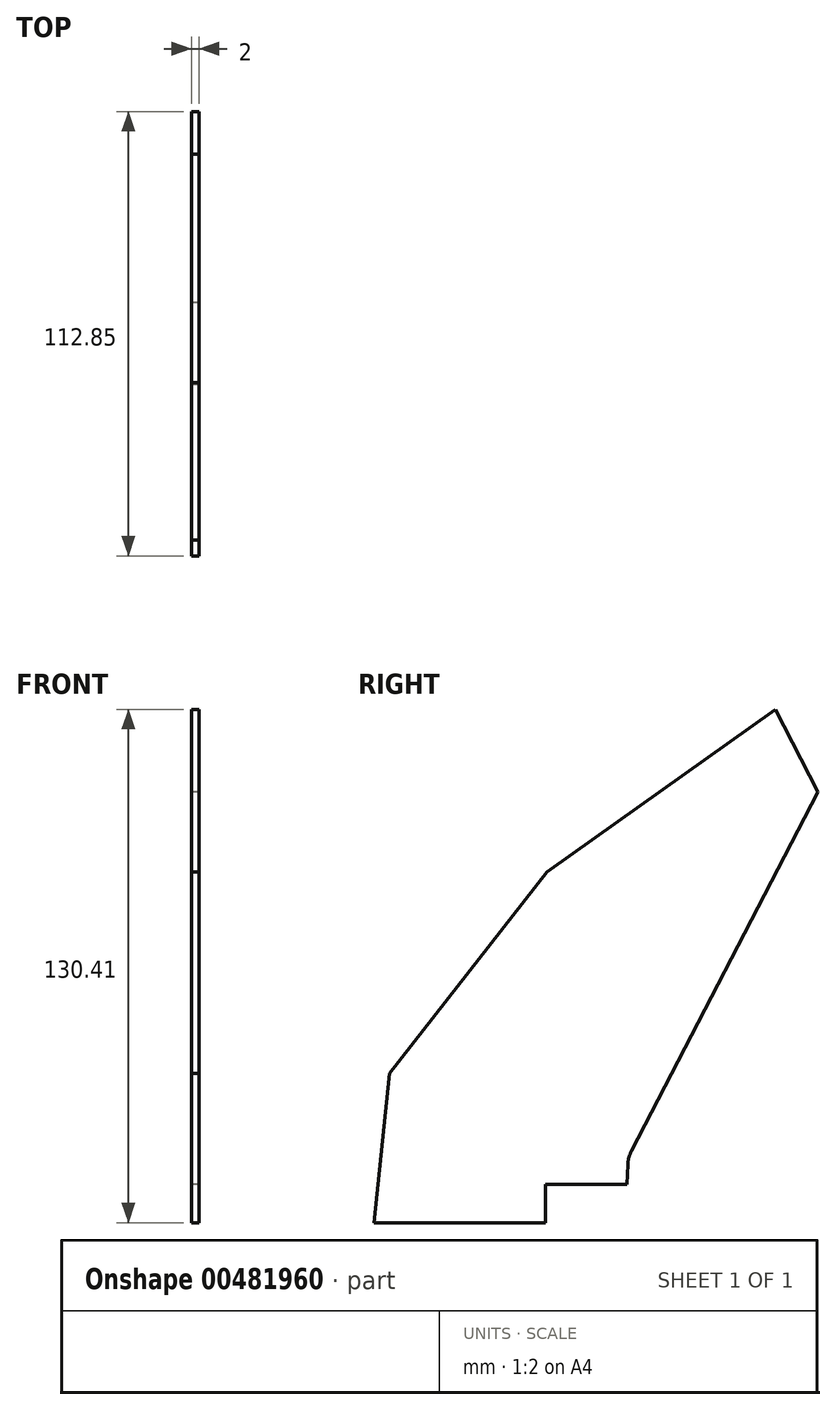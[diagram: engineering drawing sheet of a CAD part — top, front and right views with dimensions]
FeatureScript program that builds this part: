
annotation { "Feature Type Name" : "Feature", "Feature Type Description" : "" }
export const myFeature = defineFeature(function(context is Context, id is Id, definition is map)
    precondition{}
    {
        {
            var Q0;
            Q0=qCreatedBy(makeId("Right.planeOp"),FACE);
            var sketch = newSketch(context, id + "F0", { "sketchPlane" : qUnion([Q0])});
            skLineSegment(sketch, "E0", {"start": v(-134.97, 0) * mm, "end": v(-130.98, 37.94) * mm});
            skLineSegment(sketch, "E1", {"start": v(-130.98, 37.94) * mm, "end": v(-90.97, 89.16) * mm});
            skLineSegment(sketch, "E2", {"start": v(-90.97, 89.16) * mm, "end": v(-32.94, 130.41) * mm});
            skLineSegment(sketch, "E3", {"start": v(-32.94, 130.41) * mm, "end": v(-22.12, 109.48) * mm});
            skLineSegment(sketch, "E4", {"start": v(-22.12, 109.48) * mm, "end": v(-70.38, 16.58) * mm});
            skLineSegment(sketch, "E5", {"start": v(-70.38, 16.58) * mm, "end": v(-70.62, 9.78) * mm});
            skLineSegment(sketch, "E6", {"start": v(-91.4, 0) * mm, "end": v(-134.97, 0) * mm});
            skLineSegment(sketch, "E7", {"start": v(-91.4, 0) * mm, "end": v(-91.4, 9.78) * mm});
            skLineSegment(sketch, "E8", {"start": v(-91.4, 9.78) * mm, "end": v(-70.62, 9.78) * mm});
            skSolve(sketch);
        }
        {
            var Q0;
            Q0 = qSketchRegion(id + "F0", true);
            extrude(context, id + "F1", {"entities" : qUnion([Q0]), "depth" : 2 * mm});
        }
        {
            var Q0;
            Q0=makeQuery(id+"F1.opExtrude","SWEPT_EDGE",EDGE,{"disambiguationData":[OSD([sQuery(id+"F0.wireOp",EDGE,"E4"),sQuery(id+"F0.wireOp",EDGE,"E5")])]});
            fillet(context, id + "F2", {"entities" : qUnion([Q0]), "radius" : 8 * mm, "tangentPropagation" : true, "allowEdgeOverflow" : false});
        }
    });
